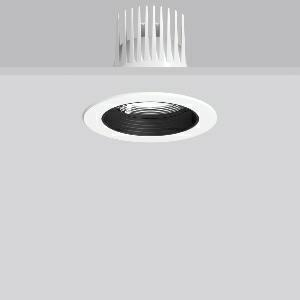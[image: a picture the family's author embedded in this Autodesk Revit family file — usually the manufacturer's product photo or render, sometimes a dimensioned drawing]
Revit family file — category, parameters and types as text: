
# Revit family: heledon_maxi_e_901769_002_1_6e53
name_source: partatom
category: Lighting Fixtures
units: mm (PartAtom-declared; Revit-internal decimal feet)

## family parameters
Cut with Voids When Loaded = No
Host = Face
Light Source = No
Part Type = Normal
Room Calculation Point = No
Round Connector Dimension = Use Diameter
Shared = No

## types (1)
- HELEDON maxi E (1 x LED Modul 940, 3800 lm, 4000)
    Apparent Load = 35 VA
    Approval mark = CE
    CIE Flux Codes = 96 100 100 100 100
    Color Rendering = 92
    Color Temperature = 4000
    Default Elevation = 1800 mm
    Description = Series: HELEDON maxi
Round recessed downlight. Housing: die-cast aluminium, powder-coated. Black plastic ring and recessed LED to prevent glare from the side. Optical assembly with lens made of plastic (polycarbonate) for the best homogeneous light distribution - can be changed without tools. Best colour rendering index Ra>90. Suitable for Recessed ceiling mounting. Installation without tools thanks to spring fastening system. Including separate LED converter with connecting cable 600 mm.High quality converter without flickering and stroboscopic effect. Through-wiring box (5 pole) available as accessory. The following accessories can be mounted without use of tools: interchangeable lenses, decorative glasses, honeycomb louvre, clear and frosted diffusers, white interchangeable plastic ring. 
Colour: traffic white, matt (RAL 9016)
Diameter: 162 mm
Height: 3 mm
Cut-out diameter: 152 mm
Recess height: 200 mm
Luminaire: recess height: 135 mm
Lamp: LED
Socket: without socket
Colour temperature: 4000K
Colour rendering index (CRI): 92
System power: 35 W
Rated luminous flux: 3800 lm
Luminous efficiency: 109 lm/W
Control gear: Regulated power supply
Protection class: II
Type of protection: IP 20
    Height = 0 mm  [stored 0 ft]
    Lamp = 1 x LED Modul 940
    Lamp Light Flux = 3800 lm
    Lamp count = 1
    Length = 162 mm
    Lifetime = 50000 h
    Luminous efficacy = 109 lm/W
    Manufacturer = RZB
    ModVariant = No
    Model = 901769.002.1
    Mounting Place = Ceiling
    Mounting Type = Recessed
    Number of Poles = 1
    OnlyDefault = Yes
    Power Factor = 1
    Product Name = HELEDON maxi E
    Product group = Recessed downlights
    ProductGroupID = 402
    Protection Class = Protection class II
    Protection Degree = IP 20
    RLX_Detail_Level = 1
    RLX_Emergency_Light_Flux = 0 lm
    RLX_Emergency_Type = 0
    RLX_Emergency_Type_DB = No
    RlxData = <blob elided: 120793 chars, md5=83c16782>
    Socket = socket
    Standby Power = 0 W
    System Light Flux = 3800 lm
    System Power = 35 W
    Type Comments = Product without accessories
    Type Image = 901663.002.jpg
    URL = http://relux.com
    VarID = ---
    Voltage = 230 V
    Voltage Range = 220-240 V
    Weight = 0.00 kg
    Width = 0 mm  [stored 0 ft]

note: [stored X ft] marks values corroborated as IEEE doubles in the binary element streams (Revit-internal decimal feet)

## geometry (parser evidence)
native form markers: Blend x4, Sweep x13
no freeform markers — native parametric forms only
